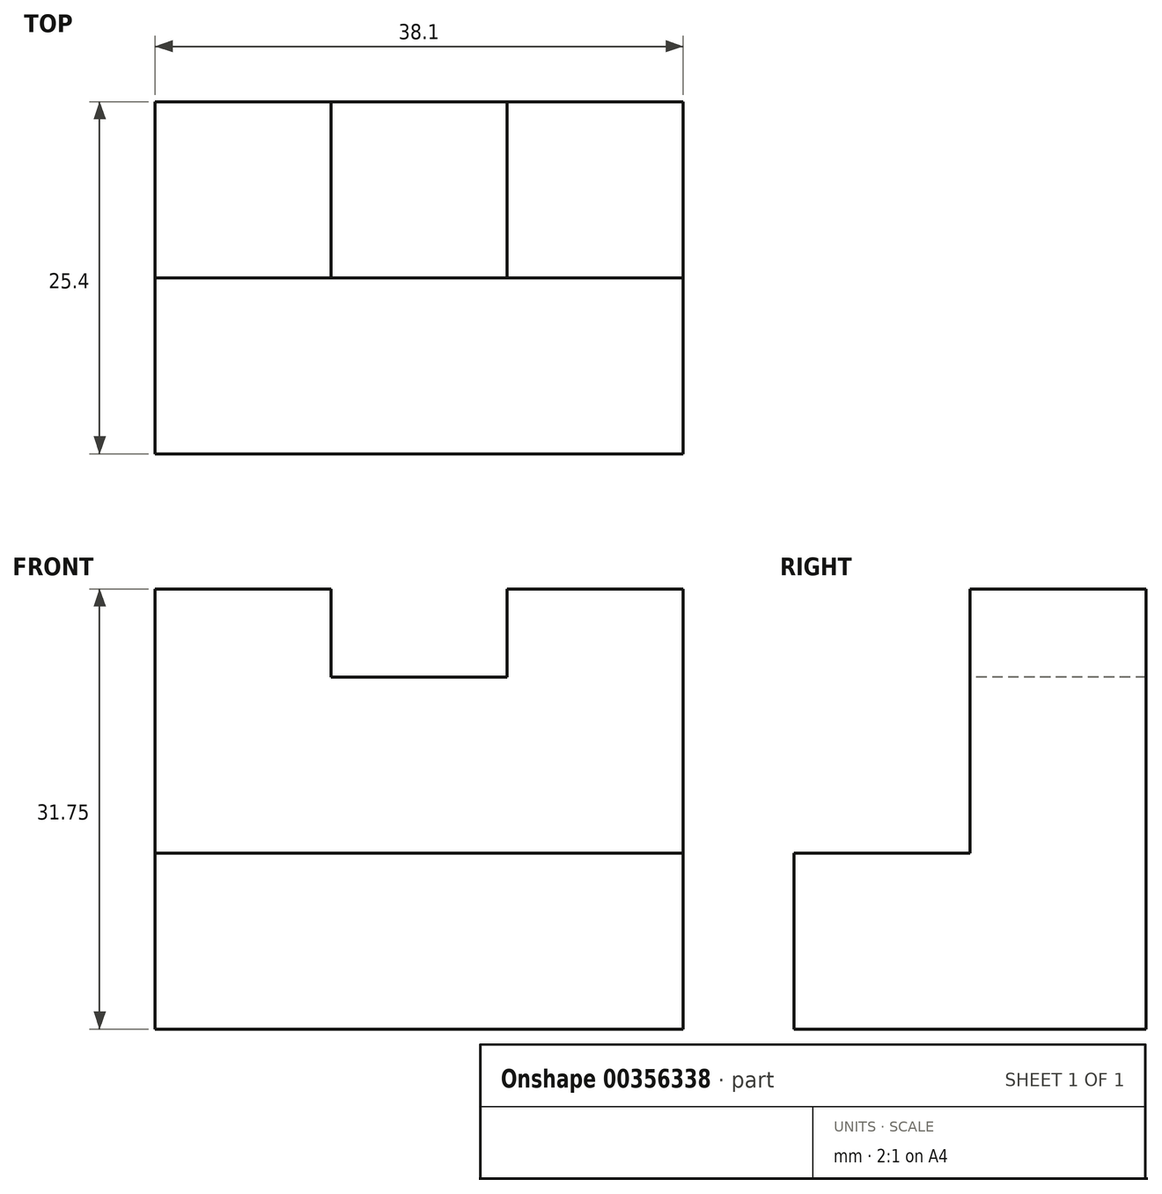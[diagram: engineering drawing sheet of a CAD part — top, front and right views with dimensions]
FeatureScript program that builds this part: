
annotation { "Feature Type Name" : "Feature", "Feature Type Description" : "" }
export const myFeature = defineFeature(function(context is Context, id is Id, definition is map)
    precondition{}
    {
        {
            var Q0;
            Q0=qCreatedBy(makeId("Right.planeOp"),FACE);
            var sketch = newSketch(context, id + "F0", { "sketchPlane" : qUnion([Q0])});
            skLineSegment(sketch, "E0", {"start": v(0, 31.75) * mm, "end": v(0, 0) * mm});
            skLineSegment(sketch, "E1", {"start": v(0, 0) * mm, "end": v(-25.4, 0) * mm});
            skLineSegment(sketch, "E2", {"start": v(-25.4, 0) * mm, "end": v(-25.4, 12.7) * mm});
            skLineSegment(sketch, "E3", {"start": v(-25.4, 12.7) * mm, "end": v(-12.7, 12.7) * mm});
            skLineSegment(sketch, "E4", {"start": v(-12.7, 12.7) * mm, "end": v(-12.7, 31.75) * mm});
            skLineSegment(sketch, "E5", {"start": v(-12.7, 31.75) * mm, "end": v(0, 31.75) * mm});
            skSolve(sketch);
        }
        {
            var Q0;
            Q0 = qSketchRegion(id + "F0", true);
            extrude(context, id + "F1", {"entities" : qUnion([Q0]), "depth" : 38.1 * mm});
        }
        {
            var Q0;
            Q0=makeQuery(id+"F1.opExtrude","SWEPT_FACE",FACE,{"disambiguationData":[OSD([sQuery(id+"F0.wireOp",EDGE,"E5")])]});
            var sketch = newSketch(context, id + "F2", { "sketchPlane" : qUnion([Q0])});
            skLineSegment(sketch, "E6", {"start": v(0, 0) * mm, "end": v(12.7, 0) * mm});
            skLineSegment(sketch, "E7", {"start": v(12.7, 0) * mm, "end": v(12.7, -12.7) * mm});
            skLineSegment(sketch, "E8", {"start": v(12.7, -12.7) * mm, "end": v(25.4, -12.7) * mm});
            skLineSegment(sketch, "E9", {"start": v(25.4, -12.7) * mm, "end": v(25.4, 0) * mm});
            skLineSegment(sketch, "E10", {"start": v(25.4, 0) * mm, "end": v(12.7, 0) * mm});
            skSolve(sketch);
        }
        {
            var Q0;
            Q0 = qSketchRegion(id + "F2", true);
            extrude(context, id + "F3", {"entities" : qUnion([Q0]), "operationType" : NewBodyOperationType.REMOVE, "oppositeDirection" : true, "depth" : 6.35 * mm});
        }
    });
